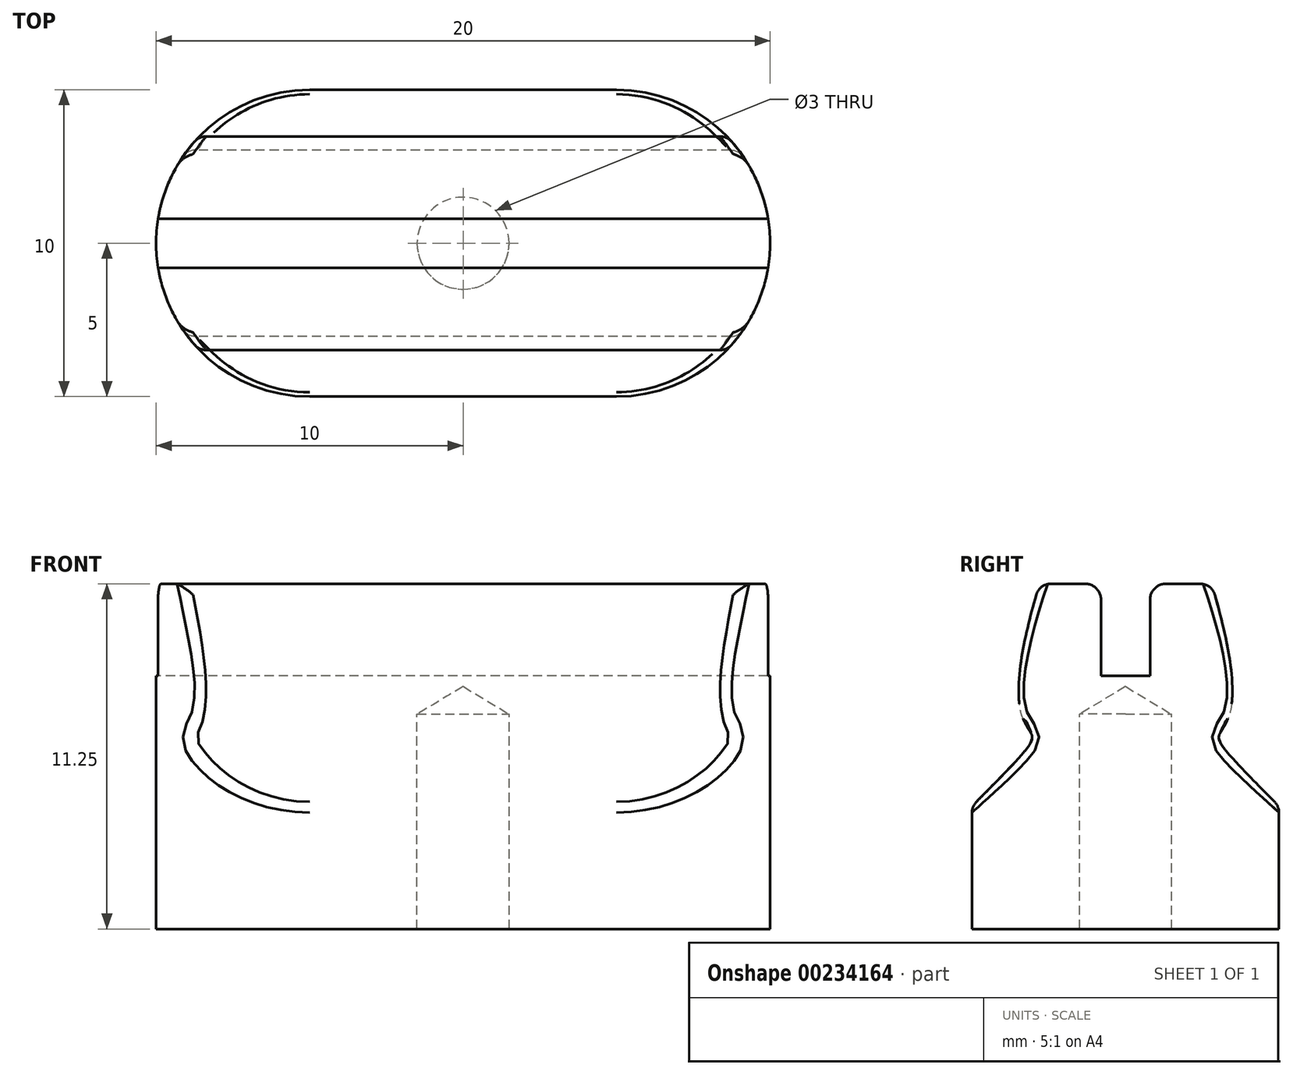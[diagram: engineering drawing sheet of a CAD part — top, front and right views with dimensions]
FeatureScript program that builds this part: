
annotation { "Feature Type Name" : "Feature", "Feature Type Description" : "" }
export const myFeature = defineFeature(function(context is Context, id is Id, definition is map)
    precondition{}
    {
        {
            var Q0;
            Q0=qCreatedBy(makeId("Right.planeOp"),FACE);
            var sketch = newSketch(context, id + "F0", { "sketchPlane" : qUnion([Q0])});
            skLineSegment(sketch, "E0.top", {"start": v(2.8, 11.25) * mm, "end": v(0.8, 11.25) * mm});
            skLineSegment(sketch, "E1.top", {"start": v(0.8, 8.25) * mm, "end": v(-0.8, 8.25) * mm});
            skLineSegment(sketch, "E1.left", {"start": v(0.8, 11.25) * mm, "end": v(0.8, 8.25) * mm});
            skLineSegment(sketch, "E1.right", {"start": v(-0.8, 11.25) * mm, "end": v(-0.8, 8.25) * mm});
            skLineSegment(sketch, "E2.left", {"start": v(5, 0) * mm, "end": v(5, 4) * mm});
            skLineSegment(sketch, "E2.right", {"start": v(-5, 0) * mm, "end": v(-5, 4) * mm});
            skLineSegment(sketch, "E3", {"start": v(-5, 0) * mm, "end": v(5, 0) * mm});
            skLineSegment(sketch, "E4.trimOffspring", {"start": v(-0.8, 11.25) * mm, "end": v(-2.8, 11.25) * mm});
            skFitSpline(sketch, "E5", {"points": [v(-2.8, 11.25) * mm, v(-5, 4) * mm], "startDerivative": vector(-6.6, -21.75) * mm, "endDerivative": vector(-12.6, -12.75) * mm});
            skFitSpline(sketch, "E6.MirrorCS", {"points": [v(2.8, 11.25) * mm, v(5, 4) * mm], "startDerivative": vector(6.6, -21.75) * mm, "endDerivative": vector(12.6, -12.75) * mm});
            skSolve(sketch);
        }
        {
            var Q0;
            Q0 = qSketchRegion(id + "F0", true);
            extrude(context, id + "F1", {"entities" : qUnion([Q0]), "depth" : 20 * mm, "symmetric" : true});
        }
        {
            var Q0;
            Q0=makeQuery(id+"F1.opExtrude","SWEPT_FACE",FACE,{"disambiguationData":[OSD([sQuery(id+"F0.wireOp",EDGE,"E3")])]});
            var sketch = newSketch(context, id + "F2", { "sketchPlane" : qUnion([Q0])});
            skArc(sketch, "E7", {"start": v(-5, 5) * mm, "mid": v(-8.54, 3.54) * mm, "end": v(-10, 0) * mm});
            skLineSegment(sketch, "E8", {"start": v(0, 5) * mm, "end": v(-10, 5) * mm, "construction": true});
            skArc(sketch, "E9.MirrorCS", {"start": v(-5, -5) * mm, "mid": v(-8.54, -3.54) * mm, "end": v(-10, 0) * mm});
            skArc(sketch, "E10.MirrorCS", {"start": v(5, 5) * mm, "mid": v(8.54, 3.54) * mm, "end": v(10, 0) * mm});
            skArc(sketch, "E11.MirrorCS", {"start": v(5, -5) * mm, "mid": v(8.54, -3.54) * mm, "end": v(10, 0) * mm});
            skLineSegment(sketch, "E12", {"start": v(-5, 5) * mm, "end": v(5, 5) * mm});
            skLineSegment(sketch, "E13", {"start": v(-5, -5) * mm, "end": v(5, -5) * mm});
            skSolve(sketch);
        }
        {
            var Q0;
            Q0 = qSketchRegion(id + "F2", true);
            extrude(context, id + "F3", {"entities" : qUnion([Q0]), "operationType" : NewBodyOperationType.INTERSECT, "endBound" : BoundingType.THROUGH_ALL, "oppositeDirection" : true, "depth" : 25 * mm});
        }
        {
            var Q0;
            Q0=makeQuery(id+"F1.opExtrude","SWEPT_FACE",FACE,{"disambiguationData":[OSD([sQuery(id+"F0.wireOp",EDGE,"E3")])]});
            var sketch = newSketch(context, id + "F4", { "sketchPlane" : qUnion([Q0])});
            skPoint(sketch, "E14", {"position": v(0, 0) * mm});
            skSolve(sketch);
        }
        {
            var Q0;
            Q0=sQuery(id+"F4.wireOp",VERTEX,"E14");
            var Q1;
            Q1=makeQuery(id+"F1.opExtrude","SWEPT_BODY",BODY,{"disambiguationData":[OSD([sQuery(id+"F0.wireOp",EDGE,"E0.top"),sQuery(id+"F0.wireOp",EDGE,"E0.left"),sQuery(id+"F0.wireOp",EDGE,"E0.right"),sQuery(id+"F0.wireOp",EDGE,"E1.top"),sQuery(id+"F0.wireOp",EDGE,"E1.left"),sQuery(id+"F0.wireOp",EDGE,"E1.right"),sQuery(id+"F0.wireOp",EDGE,"E2.top"),sQuery(id+"F0.wireOp",EDGE,"E2.left"),sQuery(id+"F0.wireOp",EDGE,"E2.right"),sQuery(id+"F0.wireOp",EDGE,"d7dca57b-4e73-4a62-bbb2-4629a3e0bd5a.trimOffspring"),sQuery(id+"F0.wireOp",EDGE,"E3"),sQuery(id+"F0.wireOp",EDGE,"E4.trimOffspring")])]});
            hole(context, id + "F5", {"style" : HoleStyle.SIMPLE, "endStyle" : HoleEndStyle.BLIND, "holeDiameter" : 3 * mm, "holeDepth" : 7 * mm, "locations" : qUnion([Q0]), "scope" : qUnion([Q1]), "startStyle" : HoleStartStyle.PART});
        }
        {
            var Q0;
            Q0=makeQuery(id+"F1.opExtrude","SWEPT_EDGE",EDGE,{"disambiguationData":[OSD([sQuery(id+"F0.wireOp",EDGE,"E4.trimOffspring"),sQuery(id+"F0.wireOp",EDGE,"E5")])]});
            var Q1;
            Q1=makeQuery(id+"F1.opExtrude","SWEPT_EDGE",EDGE,{"disambiguationData":[OSD([sQuery(id+"F0.wireOp",EDGE,"E1.right"),sQuery(id+"F0.wireOp",EDGE,"E4.trimOffspring")])]});
            var Q2;
            Q2=makeQuery(id+"F1.opExtrude","SWEPT_EDGE",EDGE,{"disambiguationData":[OSD([sQuery(id+"F0.wireOp",EDGE,"E0.top"),sQuery(id+"F0.wireOp",EDGE,"E1.left")])]});
            var Q3;
            Q3=makeQuery(id+"F1.opExtrude","SWEPT_EDGE",EDGE,{"disambiguationData":[OSD([sQuery(id+"F0.wireOp",EDGE,"E0.top"),sQuery(id+"F0.wireOp",EDGE,"E6.MirrorCS")])]});
            var Q4;
            Q4=makeQuery(id+"F3.boolean.opBoolean","INTERSECT",EDGE,{"derivedFrom":[makeQuery(id+"F1.opExtrude","SWEPT_FACE",FACE,{"disambiguationData":[OSD([sQuery(id+"F0.wireOp",EDGE,"E6.MirrorCS")])]}),makeQuery(id+"F3.boolean.toolComplement.opBoolean","COPY",FACE,{"derivedFrom":makeQuery(id+"F3.opExtrude","SWEPT_FACE",FACE,{"disambiguationData":[OSD([sQuery(id+"F2.wireOp",EDGE,"E10.MirrorCS"),sQuery(id+"F2.wireOp",EDGE,"E11.MirrorCS")])]})})]});
            var Q5;
            Q5=makeQuery(id+"F3.boolean.opBoolean","INTERSECT",EDGE,{"derivedFrom":[makeQuery(id+"F1.opExtrude","SWEPT_FACE",FACE,{"disambiguationData":[OSD([sQuery(id+"F0.wireOp",EDGE,"E6.MirrorCS")])]}),makeQuery(id+"F3.boolean.toolComplement.opBoolean","COPY",FACE,{"derivedFrom":makeQuery(id+"F3.opExtrude","SWEPT_FACE",FACE,{"disambiguationData":[OSD([sQuery(id+"F2.wireOp",EDGE,"E7"),sQuery(id+"F2.wireOp",EDGE,"E9.MirrorCS")])]})})]});
            var Q6;
            Q6=makeQuery(id+"F1.opExtrude","SWEPT_EDGE",EDGE,{"disambiguationData":[OSD([sQuery(id+"F0.wireOp",EDGE,"E2.left"),sQuery(id+"F0.wireOp",EDGE,"E6.MirrorCS")])]});
            var Q7;
            Q7=makeQuery(id+"F3.boolean.opBoolean","INTERSECT",EDGE,{"derivedFrom":[makeQuery(id+"F1.opExtrude","SWEPT_FACE",FACE,{"disambiguationData":[OSD([sQuery(id+"F0.wireOp",EDGE,"E5")])]}),makeQuery(id+"F3.boolean.toolComplement.opBoolean","COPY",FACE,{"derivedFrom":makeQuery(id+"F3.opExtrude","SWEPT_FACE",FACE,{"disambiguationData":[OSD([sQuery(id+"F2.wireOp",EDGE,"E10.MirrorCS"),sQuery(id+"F2.wireOp",EDGE,"E11.MirrorCS")])]})})]});
            var Q8;
            Q8=makeQuery(id+"F3.boolean.opBoolean","INTERSECT",EDGE,{"derivedFrom":[makeQuery(id+"F1.opExtrude","SWEPT_FACE",FACE,{"disambiguationData":[OSD([sQuery(id+"F0.wireOp",EDGE,"E5")])]}),makeQuery(id+"F3.boolean.toolComplement.opBoolean","COPY",FACE,{"derivedFrom":makeQuery(id+"F3.opExtrude","SWEPT_FACE",FACE,{"disambiguationData":[OSD([sQuery(id+"F2.wireOp",EDGE,"E7"),sQuery(id+"F2.wireOp",EDGE,"E9.MirrorCS")])]})})]});
            var Q9;
            Q9=makeQuery(id+"F1.opExtrude","SWEPT_EDGE",EDGE,{"disambiguationData":[OSD([sQuery(id+"F0.wireOp",EDGE,"E2.right"),sQuery(id+"F0.wireOp",EDGE,"E5")])]});
            fillet(context, id + "F6", {"entities" : qUnion([Q0, Q1, Q2, Q3, Q4, Q5, Q6, Q7, Q8, Q9]), "radius" : 0.5 * mm, "tangentPropagation" : true, "allowEdgeOverflow" : false});
        }
    });
